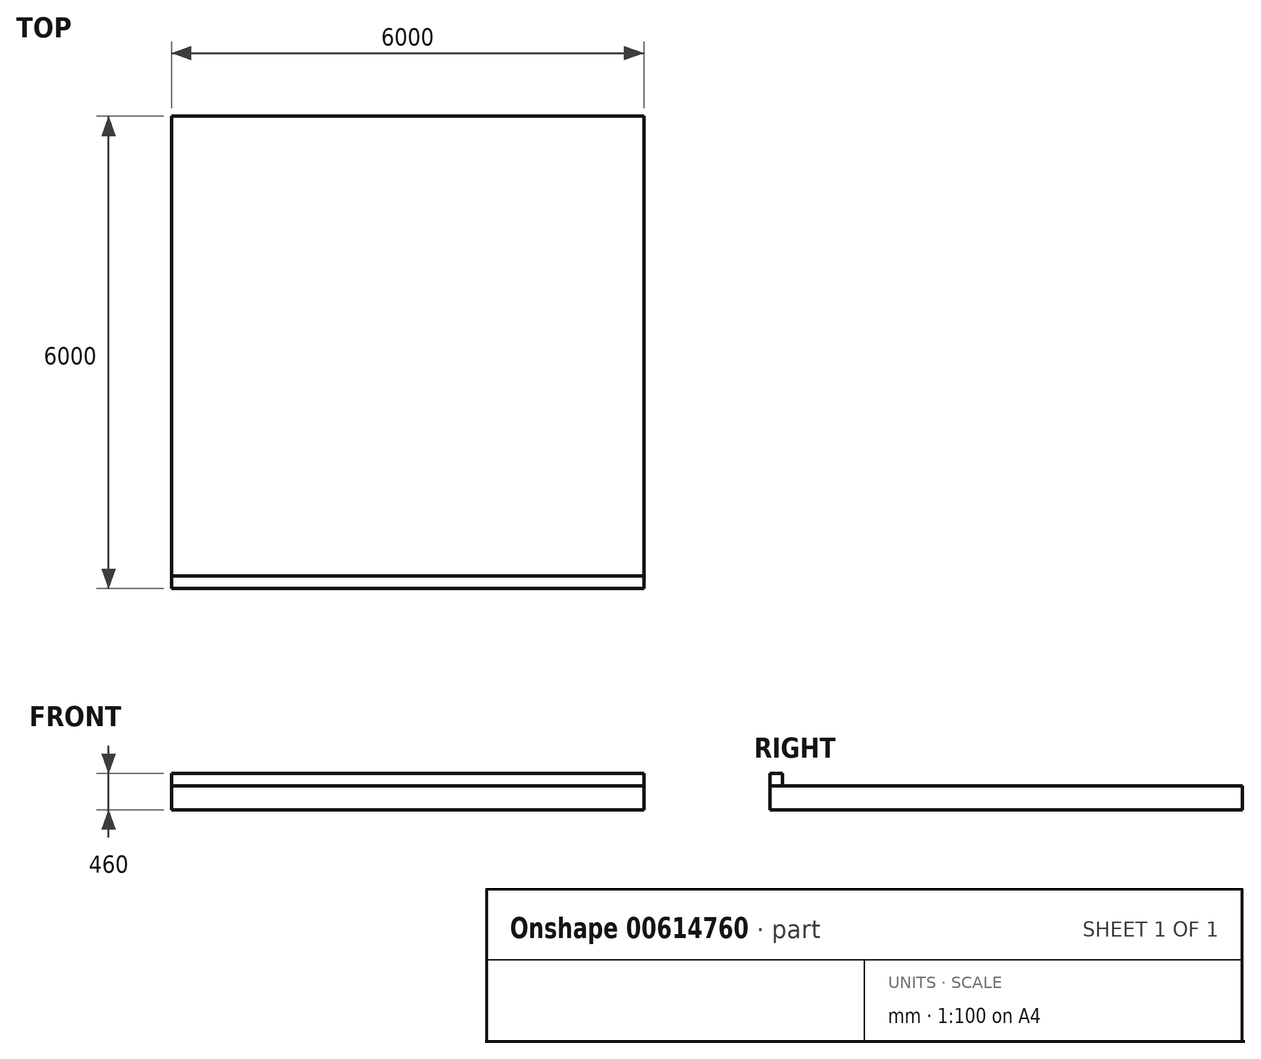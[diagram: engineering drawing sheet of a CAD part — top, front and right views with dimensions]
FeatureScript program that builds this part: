
annotation { "Feature Type Name" : "Feature", "Feature Type Description" : "" }
export const myFeature = defineFeature(function(context is Context, id is Id, definition is map)
    precondition{}
    {
        {
            var Q0;
            Q0=qCreatedBy(makeId("Top.planeOp"),FACE);
            var sketch = newSketch(context, id + "F0", { "sketchPlane" : qUnion([Q0])});
            skLineSegment(sketch, "E0.bottom", {"start": v(0, 0) * mm, "end": v(6000, 0) * mm});
            skLineSegment(sketch, "E0.top", {"start": v(0, 6000) * mm, "end": v(6000, 6000) * mm});
            skLineSegment(sketch, "E0.left", {"start": v(0, 0) * mm, "end": v(0, 6000) * mm});
            skLineSegment(sketch, "E0.right", {"start": v(6000, 0) * mm, "end": v(6000, 6000) * mm});
            skSolve(sketch);
        }
        {
            var Q0;
            Q0=makeQuery(id+"F0.imprint","IMPRINT",FACE,{"disambiguationData":[TD([[makeQuery(id+"F0.imprint","IMPRINT",EDGE,{"derivedFrom":sQuery(id+"F0.wireOp",EDGE,"E0.bottom")}),1.0]])]});
            extrude(context, id + "F1", {"entities" : qUnion([Q0]), "depth" : 300 * mm, "offsetDistance" : 25 * mm});
        }
        {
            var Q0;
            Q0=makeQuery(id+"F1.opExtrude","SWEPT_FACE",FACE,{"disambiguationData":[OSD([sQuery(id+"F0.wireOp",EDGE,"E0.bottom")])]});
            var sketch = newSketch(context, id + "F2", { "sketchPlane" : qUnion([Q0])});
            skLineSegment(sketch, "E1.bottom", {"start": v(0, 300) * mm, "end": v(6000, 300) * mm});
            skLineSegment(sketch, "E1.top", {"start": v(0, 460) * mm, "end": v(6000, 460) * mm});
            skLineSegment(sketch, "E1.left", {"start": v(0, 300) * mm, "end": v(0, 460) * mm});
            skLineSegment(sketch, "E1.right", {"start": v(6000, 300) * mm, "end": v(6000, 460) * mm});
            skSolve(sketch);
        }
        {
            var Q0;
            Q0=makeQuery(id+"F2.imprint","IMPRINT",FACE,{"disambiguationData":[TD([[makeQuery(id+"F2.imprint","IMPRINT",EDGE,{"derivedFrom":sQuery(id+"F2.wireOp",EDGE,"E1.bottom")}),1.0]])]});
            extrude(context, id + "F3", {"entities" : qUnion([Q0]), "oppositeDirection" : true, "depth" : 160 * mm, "offsetDistance" : 25 * mm});
        }
    });
